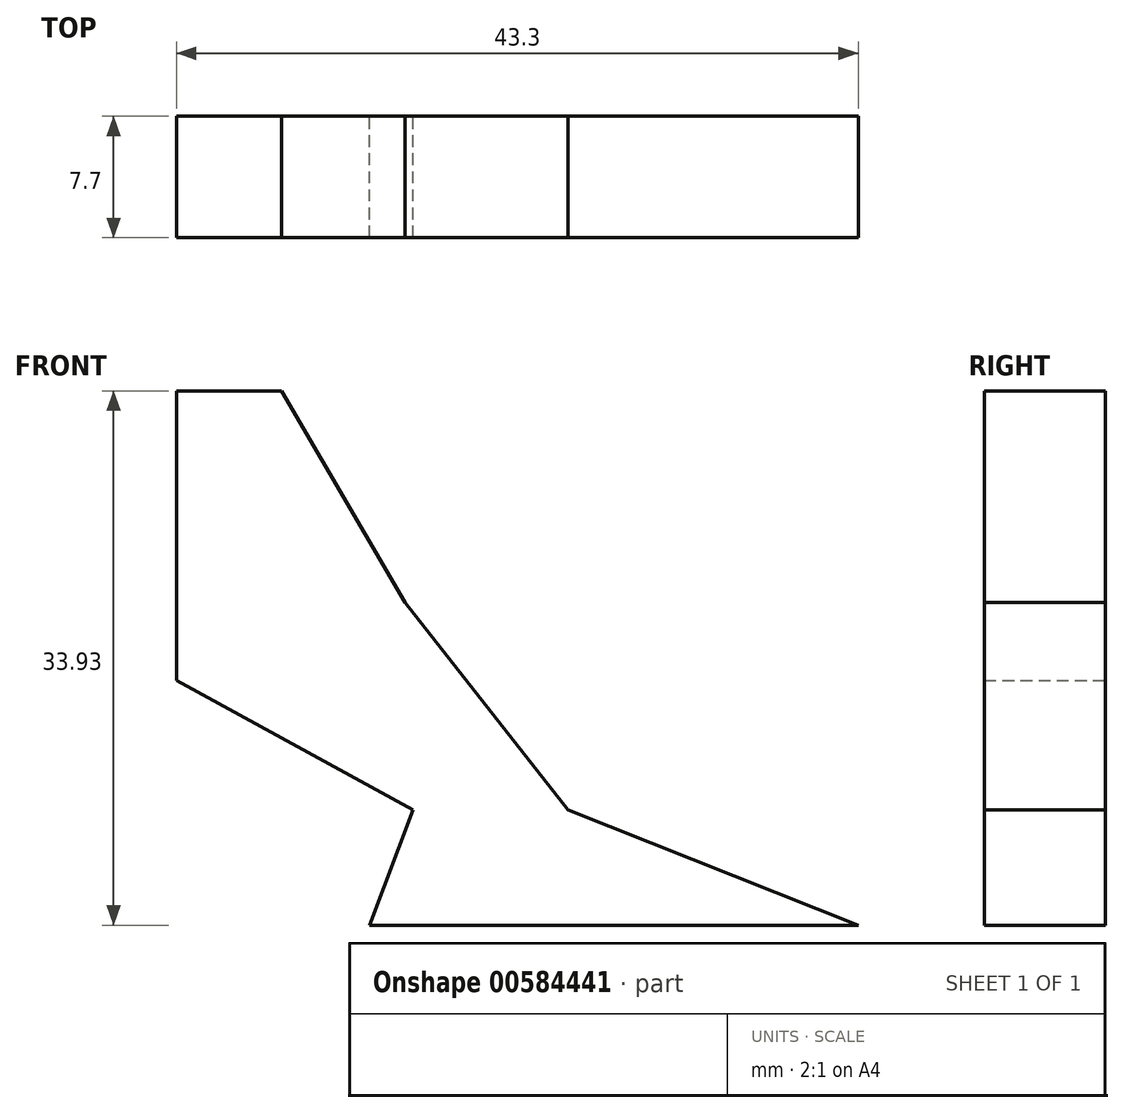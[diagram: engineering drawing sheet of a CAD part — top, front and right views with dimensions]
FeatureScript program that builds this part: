
annotation { "Feature Type Name" : "Feature", "Feature Type Description" : "" }
export const myFeature = defineFeature(function(context is Context, id is Id, definition is map)
    precondition{}
    {
        {
            var Q0;
            Q0=qCreatedBy(makeId("Front.planeOp"),FACE);
            var sketch = newSketch(context, id + "F0", { "sketchPlane" : qUnion([Q0])});
            skLineSegment(sketch, "E0", {"start": v(-36.76, 13.43) * mm, "end": v(-31.57, -1.86) * mm});
            skLineSegment(sketch, "E1", {"start": v(-31.57, -1.86) * mm, "end": v(-21.74, -13.16) * mm});
            skLineSegment(sketch, "E2", {"start": v(-21.74, -13.16) * mm, "end": v(-11.9, -13.16) * mm});
            skLineSegment(sketch, "E3", {"start": v(-11.9, -13.16) * mm, "end": v(-22.27, 0) * mm});
            skLineSegment(sketch, "E4", {"start": v(-22.27, 0) * mm, "end": v(-30.1, 13.43) * mm});
            skLineSegment(sketch, "E5", {"start": v(-30.1, 13.43) * mm, "end": v(-36.76, 13.43) * mm});
            skLineSegment(sketch, "E6", {"start": v(-21.74, -13.16) * mm, "end": v(-5.28, -20.5) * mm});
            skLineSegment(sketch, "E7", {"start": v(-5.28, -20.5) * mm, "end": v(6.54, -20.5) * mm});
            skLineSegment(sketch, "E8", {"start": v(6.54, -20.5) * mm, "end": v(-11.9, -13.16) * mm});
            skLineSegment(sketch, "E9", {"start": v(-21.74, -20.5) * mm, "end": v(-24.52, -20.5) * mm});
            skLineSegment(sketch, "E10", {"start": v(-24.52, -20.5) * mm, "end": v(-21.74, -13.16) * mm});
            skLineSegment(sketch, "E11", {"start": v(-15.54, -15.92) * mm, "end": v(-21.74, -20.5) * mm});
            skLineSegment(sketch, "E12", {"start": v(-21.74, -20.5) * mm, "end": v(-5.28, -20.5) * mm});
            skLineSegment(sketch, "E13", {"start": v(-36.76, 13.43) * mm, "end": v(-36.76, -4.96) * mm});
            skLineSegment(sketch, "E14", {"start": v(-36.76, -4.96) * mm, "end": v(-21.74, -13.16) * mm});
            skSolve(sketch);
        }
        {
            var Q0;
            Q0 = qSketchRegion(id + "F0", true);
            extrude(context, id + "F1", {"entities" : qUnion([Q0]), "depth" : 7.7 * mm, "offsetDistance" : 25 * mm});
        }
    });
